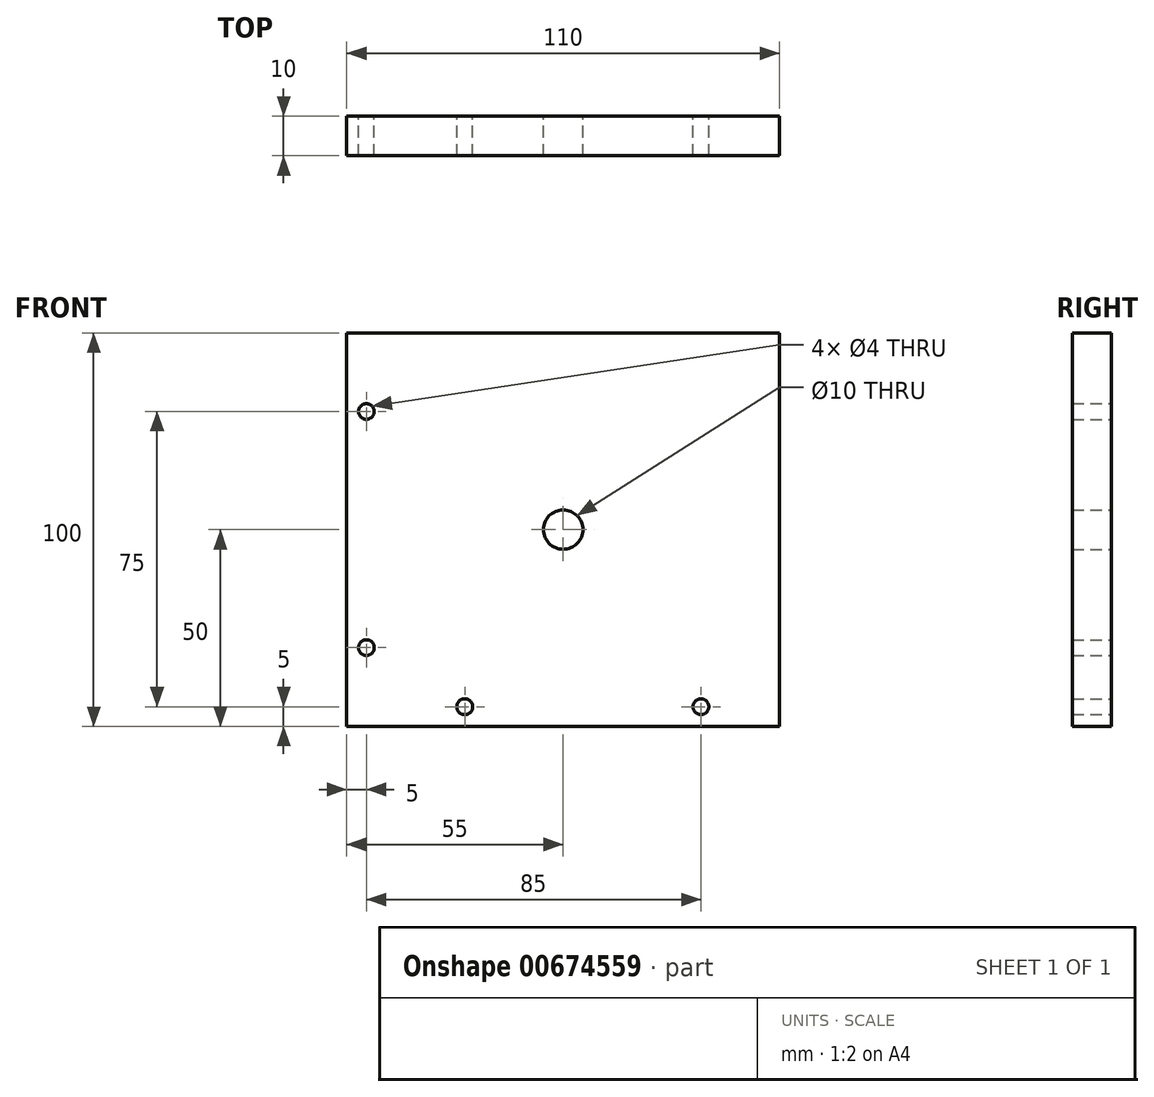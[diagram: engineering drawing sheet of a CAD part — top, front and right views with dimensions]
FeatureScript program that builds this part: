
annotation { "Feature Type Name" : "Feature", "Feature Type Description" : "" }
export const myFeature = defineFeature(function(context is Context, id is Id, definition is map)
    precondition{}
    {
        {
            var Q0;
            Q0=qCreatedBy(makeId("Front.planeOp"),FACE);
            var sketch = newSketch(context, id + "F0", { "sketchPlane" : qUnion([Q0])});
            skLineSegment(sketch, "E0.bottom", {"start": v(55, 50) * mm, "end": v(-55, 50) * mm});
            skLineSegment(sketch, "E0.top", {"start": v(55, -50) * mm, "end": v(-55, -50) * mm});
            skLineSegment(sketch, "E0.left", {"start": v(55, 50) * mm, "end": v(55, -50) * mm});
            skLineSegment(sketch, "E0.right", {"start": v(-55, 50) * mm, "end": v(-55, -50) * mm});
            skPoint(sketch, "E0.middle", {"position": v(0, 0) * mm});
            skCircle(sketch, "E1", {"center": v(0, 0) * mm, "radius": 5 * mm});
            skCircle(sketch, "E2", {"center": v(-25, -45) * mm, "radius": 2 * mm});
            skCircle(sketch, "E3", {"center": v(35, -45) * mm, "radius": 2 * mm});
            skCircle(sketch, "E4", {"center": v(-50, 30) * mm, "radius": 2 * mm});
            skCircle(sketch, "E5", {"center": v(-50, -30) * mm, "radius": 2 * mm});
            skSolve(sketch);
        }
        {
            var Q0;
            Q0=makeQuery(id+"F0.imprint","IMPRINT",FACE,{"disambiguationData":[TD([[makeQuery(id+"F0.imprint","IMPRINT",EDGE,{"derivedFrom":sQuery(id+"F0.wireOp",EDGE,"E0.bottom")}),1.0]])]});
            extrude(context, id + "F1", {"entities" : qUnion([Q0]), "depth" : 10 * mm, "offsetDistance" : 25 * mm});
        }
    });
